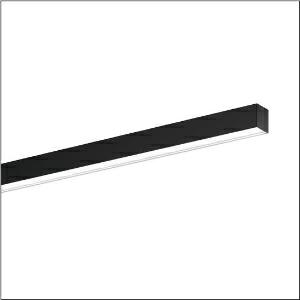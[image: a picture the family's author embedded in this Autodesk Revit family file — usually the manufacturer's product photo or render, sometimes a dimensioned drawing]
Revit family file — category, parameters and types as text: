
# Revit family: silica_r__21_51mx20tbt2b_b214
name_source: partatom
category: Lighting Fixtures
units: mm (PartAtom-declared; Revit-internal decimal feet)

## family parameters
Cut with Voids When Loaded = No
Host = Face
Light Source = No
Part Type = Normal
Room Calculation Point = No
Round Connector Dimension = Use Diameter
Shared = No

## types (1)
- --- (1 x LED, 3000 lm, 25.6 W, 6500K)
    Apparent Load = 26 VA
    CIE Flux Codes = 48 79 96 100 100
    Color Rendering = 80
    Color Temperature = 6500K
    Default Elevation = 1800 mm
    Description = Silica® 21, office luminaire, primary optical cover: cover, of PMMA, opal, light emission: direct distribution, primary light characteristic: symmetric, installation type: surface-mounted, LED, rated luminous flux: 3.000lm, luminous efficacy: 112lm/W, light colour: 8tw, colour temperature: 2700..6500K, control gear: ECG DALI, with terminal, 3+2-pole, max. 2.5mm², mains connection: 220..240V, AC, 50/60Hz, rated input power: 26.9W, luminaire housing, of aluminium, jet black (RAL 9005), length: 1.504mm, width: 53mm, height: 53mm, protection rating (complete): IP20, insulation class (complete): insulation class I (protective earthing), certification: CE, permissible operating ambient temperature: 0..+35°C, standard: EN 50419, packaging unit: 1 piece
    Height = 0 mm  [stored 0 ft]
    Lamp = 1 x LED
    Lamp Light Flux = 3000 lm
    Lamp Power = 25.6 W
    Lamp count = 1
    Length = 1504 mm
    Luminous efficacy = 117 lm/W
    Manufacturer = Siteco
    ModVariant = No
    Model = 51MX20TBT2B
    Mounting Place = Ceiling
    Mounting Type = Recessed
    Number of Poles = 1
    OnlyDefault = Yes
    Power Factor = 1
    Product Name = Silica® 21
    Product group = office luminaire | ceiling recessed
    ProductGroupID = 401
    Protection Class = Protection class I
    Protection Degree = IP 20
    RLX_Detail_Level = 1
    RLX_Emergency_Light_Flux = 0 lm
    RLX_Emergency_Type = 0
    RLX_Emergency_Type_DB = No
    RlxData = <blob elided: 25777 chars, md5=05468fc9>
    Socket = socket
    Standby Power = 0 W
    System Light Flux = 3000 lm
    System Power = 26 W
    Type Comments = individual setting
    Type Image = l_1297760.jpg
    URL = http://relux.com
    VarID = @adj_071011
    Voltage = 0 V
    Weight = 0.00 kg
    Width = 53 mm

note: [stored X ft] marks values corroborated as IEEE doubles in the binary element streams (Revit-internal decimal feet)

## geometry (parser evidence)
native form markers: Blend x4, Sweep x10
no freeform markers — native parametric forms only
